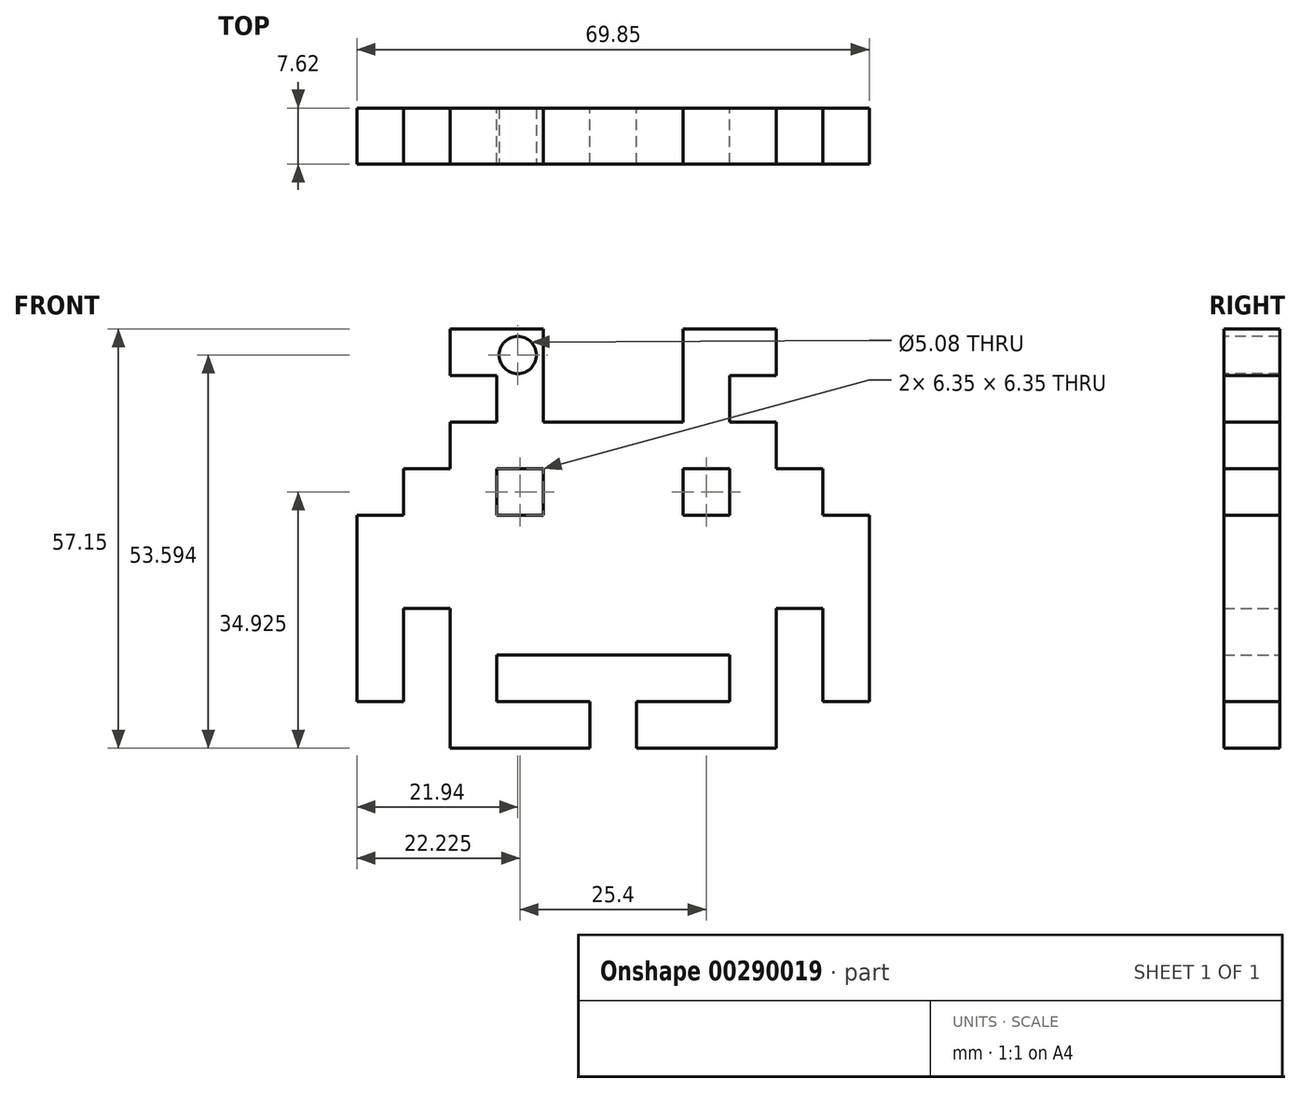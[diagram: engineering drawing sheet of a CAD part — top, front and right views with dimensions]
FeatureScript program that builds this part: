
annotation { "Feature Type Name" : "Feature", "Feature Type Description" : "" }
export const myFeature = defineFeature(function(context is Context, id is Id, definition is map)
    precondition{}
    {
        {
            var Q0;
            Q0=qCreatedBy(makeId("Front.planeOp"),FACE);
            var sketch = newSketch(context, id + "F0", { "sketchPlane" : qUnion([Q0])});
            skLineSegment(sketch, "E0", {"start": v(0, 0) * mm, "end": v(-19.05, 0) * mm});
            skLineSegment(sketch, "E1", {"start": v(-19.05, 0) * mm, "end": v(-19.05, 19.05) * mm});
            skLineSegment(sketch, "E2", {"start": v(-19.05, 19.05) * mm, "end": v(-25.4, 19.05) * mm});
            skLineSegment(sketch, "E3", {"start": v(-25.4, 19.05) * mm, "end": v(-25.4, 6.35) * mm});
            skLineSegment(sketch, "E4", {"start": v(-25.4, 6.35) * mm, "end": v(-31.75, 6.35) * mm});
            skLineSegment(sketch, "E5", {"start": v(-31.75, 6.35) * mm, "end": v(-31.75, 31.75) * mm});
            skLineSegment(sketch, "E6", {"start": v(-31.75, 31.75) * mm, "end": v(-25.4, 31.75) * mm});
            skLineSegment(sketch, "E7", {"start": v(-25.4, 31.75) * mm, "end": v(-25.4, 38.1) * mm});
            skLineSegment(sketch, "E8", {"start": v(-25.4, 38.1) * mm, "end": v(-19.05, 38.1) * mm});
            skLineSegment(sketch, "E9", {"start": v(-19.05, 38.1) * mm, "end": v(-19.05, 44.45) * mm});
            skLineSegment(sketch, "E10", {"start": v(-19.05, 44.45) * mm, "end": v(-12.7, 44.45) * mm});
            skLineSegment(sketch, "E11", {"start": v(-12.7, 44.45) * mm, "end": v(-12.7, 50.8) * mm});
            skLineSegment(sketch, "E12", {"start": v(-12.7, 50.8) * mm, "end": v(-19.05, 50.8) * mm});
            skLineSegment(sketch, "E13", {"start": v(-19.05, 50.8) * mm, "end": v(-19.05, 57.15) * mm});
            skLineSegment(sketch, "E14", {"start": v(-19.05, 57.15) * mm, "end": v(-6.35, 57.15) * mm});
            skLineSegment(sketch, "E15", {"start": v(-6.35, 57.15) * mm, "end": v(-6.35, 44.45) * mm});
            skLineSegment(sketch, "E16", {"start": v(-6.35, 44.45) * mm, "end": v(12.7, 44.45) * mm});
            skLineSegment(sketch, "E17", {"start": v(12.7, 44.45) * mm, "end": v(12.7, 57.15) * mm});
            skLineSegment(sketch, "E18", {"start": v(12.7, 57.15) * mm, "end": v(25.4, 57.15) * mm});
            skLineSegment(sketch, "E19", {"start": v(25.4, 57.15) * mm, "end": v(25.4, 50.8) * mm});
            skLineSegment(sketch, "E20", {"start": v(25.4, 50.8) * mm, "end": v(19.05, 50.8) * mm});
            skLineSegment(sketch, "E21", {"start": v(19.05, 50.8) * mm, "end": v(19.05, 44.45) * mm});
            skLineSegment(sketch, "E22", {"start": v(19.05, 44.45) * mm, "end": v(25.4, 44.45) * mm});
            skLineSegment(sketch, "E23", {"start": v(25.4, 44.45) * mm, "end": v(25.4, 38.1) * mm});
            skLineSegment(sketch, "E24", {"start": v(25.4, 38.1) * mm, "end": v(31.75, 38.1) * mm});
            skLineSegment(sketch, "E25", {"start": v(31.75, 38.1) * mm, "end": v(31.75, 31.75) * mm});
            skLineSegment(sketch, "E26", {"start": v(31.75, 31.75) * mm, "end": v(38.1, 31.75) * mm});
            skLineSegment(sketch, "E27", {"start": v(38.1, 31.75) * mm, "end": v(38.1, 6.35) * mm});
            skLineSegment(sketch, "E28", {"start": v(38.1, 6.35) * mm, "end": v(31.75, 6.35) * mm});
            skLineSegment(sketch, "E29", {"start": v(31.75, 6.35) * mm, "end": v(31.75, 19.05) * mm});
            skLineSegment(sketch, "E30", {"start": v(31.75, 19.05) * mm, "end": v(25.4, 19.05) * mm});
            skLineSegment(sketch, "E31", {"start": v(25.4, 19.05) * mm, "end": v(25.4, 0) * mm});
            skLineSegment(sketch, "E32", {"start": v(25.4, 0) * mm, "end": v(6.35, 0) * mm});
            skLineSegment(sketch, "E33", {"start": v(6.35, 0) * mm, "end": v(6.35, 6.35) * mm});
            skLineSegment(sketch, "E34", {"start": v(6.35, 6.35) * mm, "end": v(19.05, 6.35) * mm});
            skLineSegment(sketch, "E35", {"start": v(19.05, 6.35) * mm, "end": v(19.05, 12.7) * mm});
            skLineSegment(sketch, "E36", {"start": v(19.05, 12.7) * mm, "end": v(-12.7, 12.7) * mm});
            skLineSegment(sketch, "E37", {"start": v(-12.7, 12.7) * mm, "end": v(-12.7, 6.35) * mm});
            skLineSegment(sketch, "E38", {"start": v(-12.7, 6.35) * mm, "end": v(0, 6.35) * mm});
            skLineSegment(sketch, "E39", {"start": v(0, 6.35) * mm, "end": v(0, 0) * mm});
            skSolve(sketch);
        }
        {
            var Q0;
            Q0 = qSketchRegion(id + "F0", true);
            extrude(context, id + "F1", {"entities" : qUnion([Q0]), "depth" : 7.62 * mm});
        }
        {
            var Q0;
            Q0=makeQuery(id+"F1.opExtrude","CAP_FACE",FACE,{"disambiguationData":[OSD([sQuery(id+"F0.wireOp",EDGE,"E0"),sQuery(id+"F0.wireOp",EDGE,"E1"),sQuery(id+"F0.wireOp",EDGE,"E2"),sQuery(id+"F0.wireOp",EDGE,"E3"),sQuery(id+"F0.wireOp",EDGE,"E4"),sQuery(id+"F0.wireOp",EDGE,"E5"),sQuery(id+"F0.wireOp",EDGE,"E6"),sQuery(id+"F0.wireOp",EDGE,"E7"),sQuery(id+"F0.wireOp",EDGE,"E8"),sQuery(id+"F0.wireOp",EDGE,"E9"),sQuery(id+"F0.wireOp",EDGE,"E10"),sQuery(id+"F0.wireOp",EDGE,"E11"),sQuery(id+"F0.wireOp",EDGE,"E12"),sQuery(id+"F0.wireOp",EDGE,"E13"),sQuery(id+"F0.wireOp",EDGE,"E14"),sQuery(id+"F0.wireOp",EDGE,"E15"),sQuery(id+"F0.wireOp",EDGE,"E16"),sQuery(id+"F0.wireOp",EDGE,"E17"),sQuery(id+"F0.wireOp",EDGE,"E18"),sQuery(id+"F0.wireOp",EDGE,"E19"),sQuery(id+"F0.wireOp",EDGE,"E20"),sQuery(id+"F0.wireOp",EDGE,"E21"),sQuery(id+"F0.wireOp",EDGE,"E22"),sQuery(id+"F0.wireOp",EDGE,"E23"),sQuery(id+"F0.wireOp",EDGE,"E24"),sQuery(id+"F0.wireOp",EDGE,"E25"),sQuery(id+"F0.wireOp",EDGE,"E26"),sQuery(id+"F0.wireOp",EDGE,"E27"),sQuery(id+"F0.wireOp",EDGE,"E28"),sQuery(id+"F0.wireOp",EDGE,"E29"),sQuery(id+"F0.wireOp",EDGE,"E30"),sQuery(id+"F0.wireOp",EDGE,"E31"),sQuery(id+"F0.wireOp",EDGE,"E32"),sQuery(id+"F0.wireOp",EDGE,"E33"),sQuery(id+"F0.wireOp",EDGE,"E34"),sQuery(id+"F0.wireOp",EDGE,"E35"),sQuery(id+"F0.wireOp",EDGE,"E36"),sQuery(id+"F0.wireOp",EDGE,"E37"),sQuery(id+"F0.wireOp",EDGE,"E38"),sQuery(id+"F0.wireOp",EDGE,"E39")])],"isStart":false});
            var sketch = newSketch(context, id + "F2", { "sketchPlane" : qUnion([Q0])});
            skPoint(sketch, "E40.firstSnap0", {"position": v(28.57, 38.1) * mm});
            skLineSegment(sketch, "E40.bottom", {"start": v(-12.7, 38.1) * mm, "end": v(-6.35, 38.1) * mm});
            skLineSegment(sketch, "E40.top", {"start": v(-12.7, 31.75) * mm, "end": v(-6.35, 31.75) * mm});
            skLineSegment(sketch, "E40.left", {"start": v(-12.7, 38.1) * mm, "end": v(-12.7, 31.75) * mm});
            skLineSegment(sketch, "E40.right", {"start": v(-6.35, 38.1) * mm, "end": v(-6.35, 31.75) * mm});
            skLineSegment(sketch, "E41.bottom", {"start": v(19.05, 38.1) * mm, "end": v(12.7, 38.1) * mm});
            skLineSegment(sketch, "E41.top", {"start": v(19.05, 31.75) * mm, "end": v(12.7, 31.75) * mm});
            skLineSegment(sketch, "E41.left", {"start": v(19.05, 38.1) * mm, "end": v(19.05, 31.75) * mm});
            skLineSegment(sketch, "E41.right", {"start": v(12.7, 38.1) * mm, "end": v(12.7, 31.75) * mm});
            skSolve(sketch);
        }
        {
            var Q0;
            Q0 = qSketchRegion(id + "F2", true);
            extrude(context, id + "F3", {"entities" : qUnion([Q0]), "operationType" : NewBodyOperationType.REMOVE, "oppositeDirection" : true, "depth" : 7.62 * mm});
        }
        {
            var Q0;
            Q0=makeQuery(id+"F1.opExtrude","CAP_FACE",FACE,{"disambiguationData":[OSD([sQuery(id+"F0.wireOp",EDGE,"E0"),sQuery(id+"F0.wireOp",EDGE,"E1"),sQuery(id+"F0.wireOp",EDGE,"E2"),sQuery(id+"F0.wireOp",EDGE,"E3"),sQuery(id+"F0.wireOp",EDGE,"E4"),sQuery(id+"F0.wireOp",EDGE,"E5"),sQuery(id+"F0.wireOp",EDGE,"E6"),sQuery(id+"F0.wireOp",EDGE,"E7"),sQuery(id+"F0.wireOp",EDGE,"E8"),sQuery(id+"F0.wireOp",EDGE,"E9"),sQuery(id+"F0.wireOp",EDGE,"E10"),sQuery(id+"F0.wireOp",EDGE,"E11"),sQuery(id+"F0.wireOp",EDGE,"E12"),sQuery(id+"F0.wireOp",EDGE,"E13"),sQuery(id+"F0.wireOp",EDGE,"E14"),sQuery(id+"F0.wireOp",EDGE,"E15"),sQuery(id+"F0.wireOp",EDGE,"E16"),sQuery(id+"F0.wireOp",EDGE,"E17"),sQuery(id+"F0.wireOp",EDGE,"E18"),sQuery(id+"F0.wireOp",EDGE,"E19"),sQuery(id+"F0.wireOp",EDGE,"E20"),sQuery(id+"F0.wireOp",EDGE,"E21"),sQuery(id+"F0.wireOp",EDGE,"E22"),sQuery(id+"F0.wireOp",EDGE,"E23"),sQuery(id+"F0.wireOp",EDGE,"E24"),sQuery(id+"F0.wireOp",EDGE,"E25"),sQuery(id+"F0.wireOp",EDGE,"E26"),sQuery(id+"F0.wireOp",EDGE,"E27"),sQuery(id+"F0.wireOp",EDGE,"E28"),sQuery(id+"F0.wireOp",EDGE,"E29"),sQuery(id+"F0.wireOp",EDGE,"E30"),sQuery(id+"F0.wireOp",EDGE,"E31"),sQuery(id+"F0.wireOp",EDGE,"E32"),sQuery(id+"F0.wireOp",EDGE,"E33"),sQuery(id+"F0.wireOp",EDGE,"E34"),sQuery(id+"F0.wireOp",EDGE,"E35"),sQuery(id+"F0.wireOp",EDGE,"E36"),sQuery(id+"F0.wireOp",EDGE,"E37"),sQuery(id+"F0.wireOp",EDGE,"E38"),sQuery(id+"F0.wireOp",EDGE,"E39")])],"isStart":false});
            var sketch = newSketch(context, id + "F4", { "sketchPlane" : qUnion([Q0])});
            skCircle(sketch, "E42", {"center": v(-9.8, 53.6) * mm, "radius": 2.54 * mm});
            skSolve(sketch);
        }
        {
            var Q0;
            Q0 = qSketchRegion(id + "F4", true);
            extrude(context, id + "F5", {"entities" : qUnion([Q0]), "operationType" : NewBodyOperationType.REMOVE, "oppositeDirection" : true, "depth" : 7.62 * mm});
        }
    });
